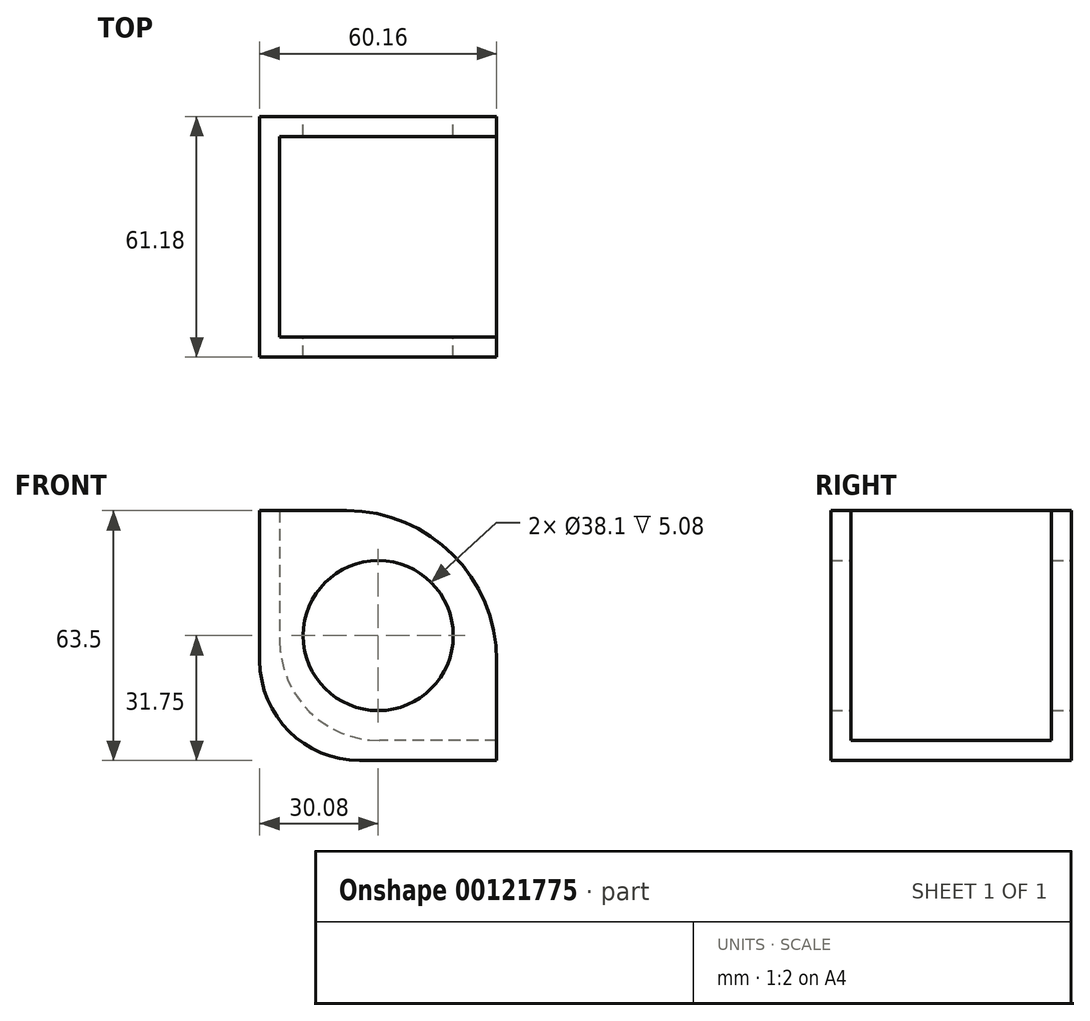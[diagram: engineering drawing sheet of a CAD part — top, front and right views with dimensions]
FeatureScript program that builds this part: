
annotation { "Feature Type Name" : "Feature", "Feature Type Description" : "" }
export const myFeature = defineFeature(function(context is Context, id is Id, definition is map)
    precondition{}
    {
        {
            var Q0;
            Q0=qCreatedBy(makeId("Top.planeOp"),FACE);
            var sketch = newSketch(context, id + "F0", { "sketchPlane" : qUnion([Q0])});
            skLineSegment(sketch, "E0.bottom", {"start": v(30.08, 30.59) * mm, "end": v(-30.08, 30.59) * mm});
            skLineSegment(sketch, "E0.top", {"start": v(30.08, -30.59) * mm, "end": v(-30.08, -30.59) * mm});
            skLineSegment(sketch, "E0.left", {"start": v(30.08, 30.59) * mm, "end": v(30.08, -30.59) * mm});
            skLineSegment(sketch, "E0.right", {"start": v(-30.08, 30.59) * mm, "end": v(-30.08, -30.59) * mm});
            skPoint(sketch, "E0.middle", {"position": v(0, 0) * mm});
            skSolve(sketch);
        }
        {
            var Q0;
            Q0=makeQuery(id+"F0.imprint","IMPRINT",FACE,{"disambiguationData":[TD([[makeQuery(id+"F0.imprint","IMPRINT",EDGE,{"derivedFrom":sQuery(id+"F0.wireOp",EDGE,"E0.bottom")}),1.0]])]});
            var Q1;
            Q1 = qSketchRegion(id + "F0", true);
            extrude(context, id + "F1", {"entities" : qUnion([Q0, Q1]), "depth" : 63.5 * mm});
        }
        {
            var Q0;
            Q0=makeQuery(id+"F1.opExtrude","SWEPT_FACE",FACE,{"disambiguationData":[OSD([sQuery(id+"F0.wireOp",EDGE,"E0.left")])]});
            var Q1;
            Q1=makeQuery(id+"F1.opExtrude","CAP_FACE",FACE,{"disambiguationData":[OSD([sQuery(id+"F0.wireOp",EDGE,"E0.bottom"),sQuery(id+"F0.wireOp",EDGE,"E0.top"),sQuery(id+"F0.wireOp",EDGE,"E0.left"),sQuery(id+"F0.wireOp",EDGE,"E0.right")])],"isStart":false});
            shell(context, id + "F2", {"entities" : qUnion([Q0, Q1]), "thickness" : 5.08 * mm});
        }
        {
            var Q0;
            Q0=makeQuery(id+"F1.opExtrude","SWEPT_FACE",FACE,{"disambiguationData":[OSD([sQuery(id+"F0.wireOp",EDGE,"E0.bottom")])]});
            var sketch = newSketch(context, id + "F3", { "sketchPlane" : qUnion([Q0])});
            skPoint(sketch, "E1", {"position": v(-30.08, 31.75) * mm});
            skPoint(sketch, "E2", {"position": v(0, 0) * mm});
            skCircle(sketch, "E3", {"center": v(0, 31.75) * mm, "radius": 19.05 * mm});
            skSolve(sketch);
        }
        {
            var Q0;
            Q0=makeQuery(id+"F3.imprint","IMPRINT",FACE,{"disambiguationData":[TD([[makeQuery(id+"F3.imprint","IMPRINT",EDGE,{"derivedFrom":sQuery(id+"F3.wireOp",EDGE,"E3")}),1.0]])]});
            var Q1;
            Q1=makeQuery(id+"F1.opExtrude","SWEPT_FACE",FACE,{"disambiguationData":[OSD([sQuery(id+"F0.wireOp",EDGE,"E0.top")])]});
            extrude(context, id + "F4", {"entities" : qUnion([Q0]), "operationType" : NewBodyOperationType.REMOVE, "endBound" : BoundingType.UP_TO_SURFACE, "oppositeDirection" : true, "endBoundEntityFace" : qUnion([Q1]), "depth" : 62.13 * mm});
        }
        {
            var Q0;
            Q0=makeQuery(id+"F1.opExtrude","CAP_EDGE",EDGE,{"disambiguationData":[OSD([sQuery(id+"F0.wireOp",EDGE,"E0.left")])],"isStart":false});
            fillet(context, id + "F5", {"entities" : qUnion([Q0]), "radius" : 38.1 * mm, "tangentPropagation" : true, "allowEdgeOverflow" : false});
        }
        {
            var Q0;
            {var subQ0=sQuery(id+"F0.wireOp",EDGE,"E0.left");Q0=makeQuery(id+"F2.opShell","OFFSET_EDGE",EDGE,{"disambiguationData":[OSD([subQ0]),TDD([makeQuery(id+"F1.opExtrude","CAP_EDGE",EDGE,{"disambiguationData":[OSD([subQ0])],"isStart":false})])]});}
            fillet(context, id + "F6", {"entities" : qUnion([Q0]), "radius" : 38.1 * mm, "tangentPropagation" : true, "allowEdgeOverflow" : false});
        }
        {
            var Q0;
            Q0=makeQuery(id+"F1.opExtrude","CAP_EDGE",EDGE,{"disambiguationData":[OSD([sQuery(id+"F0.wireOp",EDGE,"E0.right")])],"isStart":true});
            var Q1;
            {var subQ0=sQuery(id+"F0.wireOp",EDGE,"E0.right");Q1=makeQuery(id+"F2.opShell","OFFSET_EDGE",EDGE,{"disambiguationData":[OSD([subQ0]),TDD([makeQuery(id+"F1.opExtrude","CAP_EDGE",EDGE,{"disambiguationData":[OSD([subQ0])],"isStart":true})])]});}
            fillet(context, id + "F7", {"entities" : qUnion([Q0, Q1]), "radius" : 25.4 * mm, "tangentPropagation" : true, "allowEdgeOverflow" : false});
        }
    });
